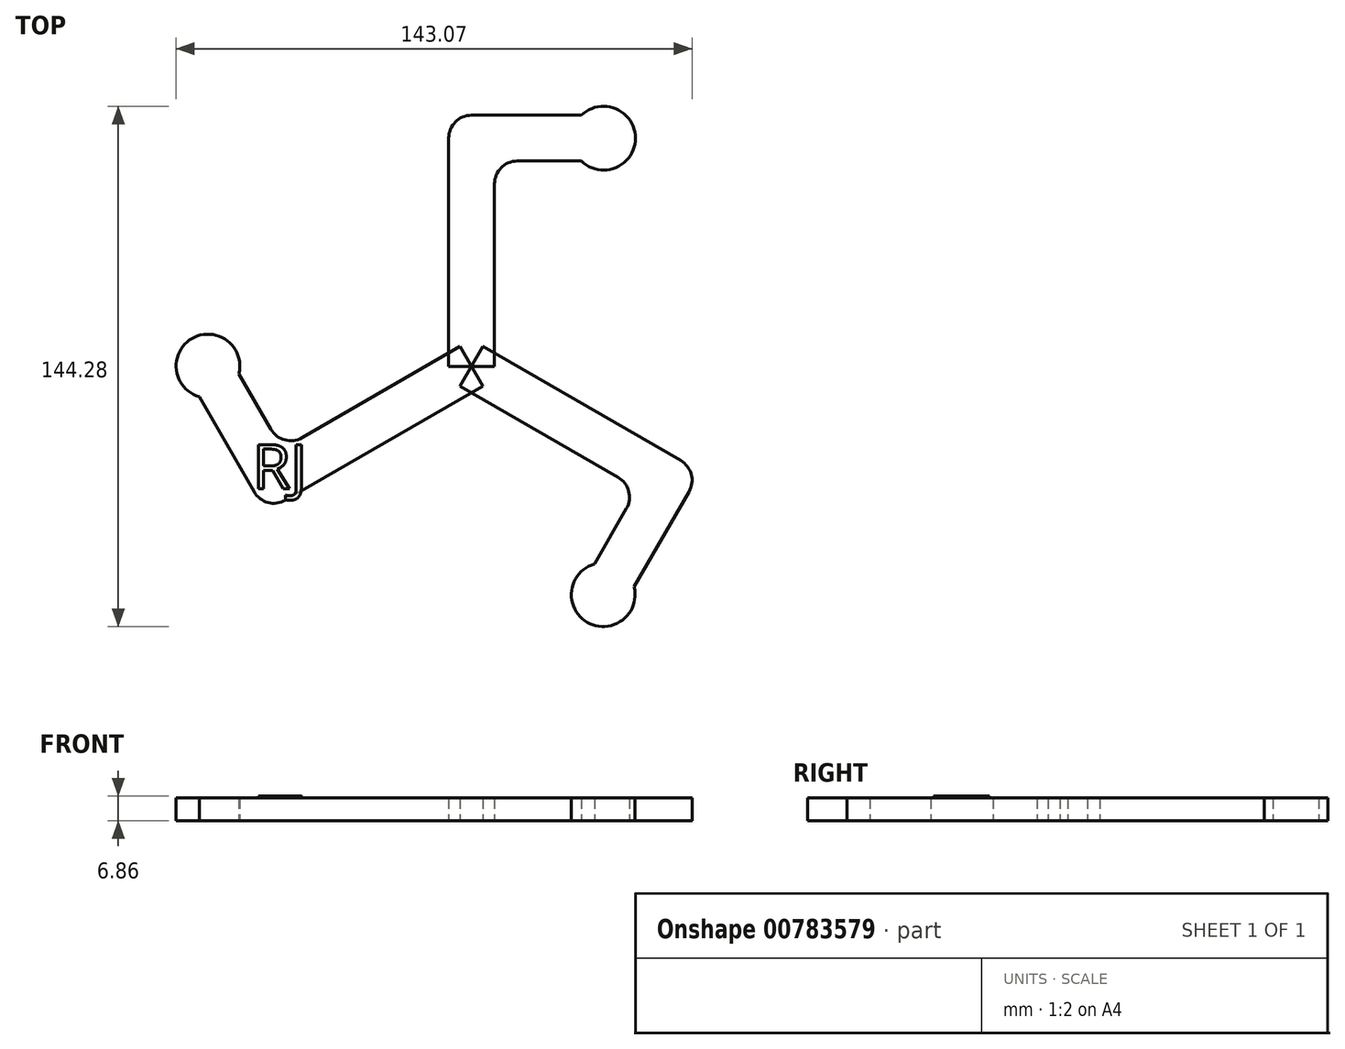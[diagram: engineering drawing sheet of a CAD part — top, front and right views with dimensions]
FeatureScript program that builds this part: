
annotation { "Feature Type Name" : "Feature", "Feature Type Description" : "" }
export const myFeature = defineFeature(function(context is Context, id is Id, definition is map)
    precondition{}
    {
        {
            var Q0;
            Q0=qCreatedBy(makeId("Top.planeOp"),FACE);
            var sketch = newSketch(context, id + "F0", { "sketchPlane" : qUnion([Q0])});
            skLineSegment(sketch, "E0", {"start": v(0, 0) * mm, "end": v(0, 63.27) * mm});
            skArc(sketch, "E1", {"start": v(30.45, 56.92) * mm, "mid": v(45.44, 63.27) * mm, "end": v(30.45, 69.62) * mm});
            skLineSegment(sketch, "E2.0", {"start": v(6.35, 0) * mm, "end": v(6.35, 50.57) * mm});
            skLineSegment(sketch, "E3.0", {"start": v(12.7, 56.92) * mm, "end": v(30.45, 56.92) * mm});
            skLineSegment(sketch, "E4.0", {"start": v(-6.35, 0) * mm, "end": v(-6.35, 63.27) * mm});
            skLineSegment(sketch, "E5.0", {"start": v(0, 69.62) * mm, "end": v(30.45, 69.62) * mm});
            skArc(sketch, "E6.filletArc", {"start": v(0, 69.62) * mm, "mid": v(-4.5, 67.76) * mm, "end": v(-6.35, 63.27) * mm});
            skArc(sketch, "E7.filletArc", {"start": v(12.7, 56.92) * mm, "mid": v(8.2, 55.06) * mm, "end": v(6.35, 50.57) * mm});
            skLineSegment(sketch, "E8", {"start": v(0, 0) * mm, "end": v(-6.35, 0) * mm});
            skLineSegment(sketch, "E9", {"start": v(6.35, 0) * mm, "end": v(0, 0) * mm});
            skSolve(sketch);
        }
        {
            var Q0;
            Q0=makeQuery(id+"F0.imprint","IMPRINT",FACE,{"disambiguationData":[TD([[makeQuery(id+"F0.imprint","IMPRINT",EDGE,{"derivedFrom":sQuery(id+"F0.wireOp",EDGE,"E1")}),1.0]])]});
            extrude(context, id + "F1", {"entities" : qUnion([Q0]), "depth" : 6.35 * mm, "offsetDistance" : 25.4 * mm});
        }
        {
            var Q0;
            Q0=qCreatedBy(makeId("Front.planeOp"),FACE);
            var sketch = newSketch(context, id + "F2", { "sketchPlane" : qUnion([Q0])});
            skLineSegment(sketch, "E10", {"start": v(0, 0) * mm, "end": v(0, 25.63) * mm});
            skSolve(sketch);
        }
        {
            var Q0;
            Q0=makeQuery(id+"F1.opExtrude","SWEPT_BODY",BODY,{"disambiguationData":[OSD([sQuery(id+"F0.wireOp",EDGE,"E1"),sQuery(id+"F0.wireOp",EDGE,"E2.0"),sQuery(id+"F0.wireOp",EDGE,"E3.0"),sQuery(id+"F0.wireOp",EDGE,"E4.0"),sQuery(id+"F0.wireOp",EDGE,"E5.0"),sQuery(id+"F0.wireOp",EDGE,"E6.filletArc"),sQuery(id+"F0.wireOp",EDGE,"E7.filletArc"),sQuery(id+"F0.wireOp",EDGE,"E8"),sQuery(id+"F0.wireOp",EDGE,"E9")])]});
            var Q1;
            Q1=sQuery(id+"F2.wireOp",EDGE,"E10");
            circularPattern(context, id + "F3", {"entities" : qUnion([Q0]), "axis" : qUnion([Q1]), "angle" : 360 * degree, "instanceCount" : 3, "oppositeDirection" : true, "equalSpace" : true});
        }
        {
            var Q0;
            Q0=makeQuery(id+"F3.opPattern","COPY",FACE,{"derivedFrom":makeQuery(id+"F1.opExtrude","CAP_FACE",FACE,{"disambiguationData":[OSD([sQuery(id+"F0.wireOp",EDGE,"E1"),sQuery(id+"F0.wireOp",EDGE,"E2.0"),sQuery(id+"F0.wireOp",EDGE,"E3.0"),sQuery(id+"F0.wireOp",EDGE,"E4.0"),sQuery(id+"F0.wireOp",EDGE,"E5.0"),sQuery(id+"F0.wireOp",EDGE,"E6.filletArc"),sQuery(id+"F0.wireOp",EDGE,"E7.filletArc"),sQuery(id+"F0.wireOp",EDGE,"E8"),sQuery(id+"F0.wireOp",EDGE,"E9")])],"isStart":false}),"instanceName":"2"});
            var sketch = newSketch(context, id + "F4", { "sketchPlane" : qUnion([Q0])});
            skText(sketch, "E11", { "text": "RJ", "fontName": "OpenSans-Regular.ttf"});
            const initialGuessF4  = {"E11": [-0.0608, -0.03394, 1, 0, 0.01233]};
            skSetInitialGuess(sketch, initialGuessF4);
            skSolve(sketch);
        }
        {
            var Q0;
            Q0 = qSketchRegion(id + "F4", true);
            extrude(context, id + "F5", {"entities" : qUnion([Q0]), "operationType" : NewBodyOperationType.ADD, "depth" : 0.5 * mm, "offsetDistance" : 25.4 * mm});
        }
    });
